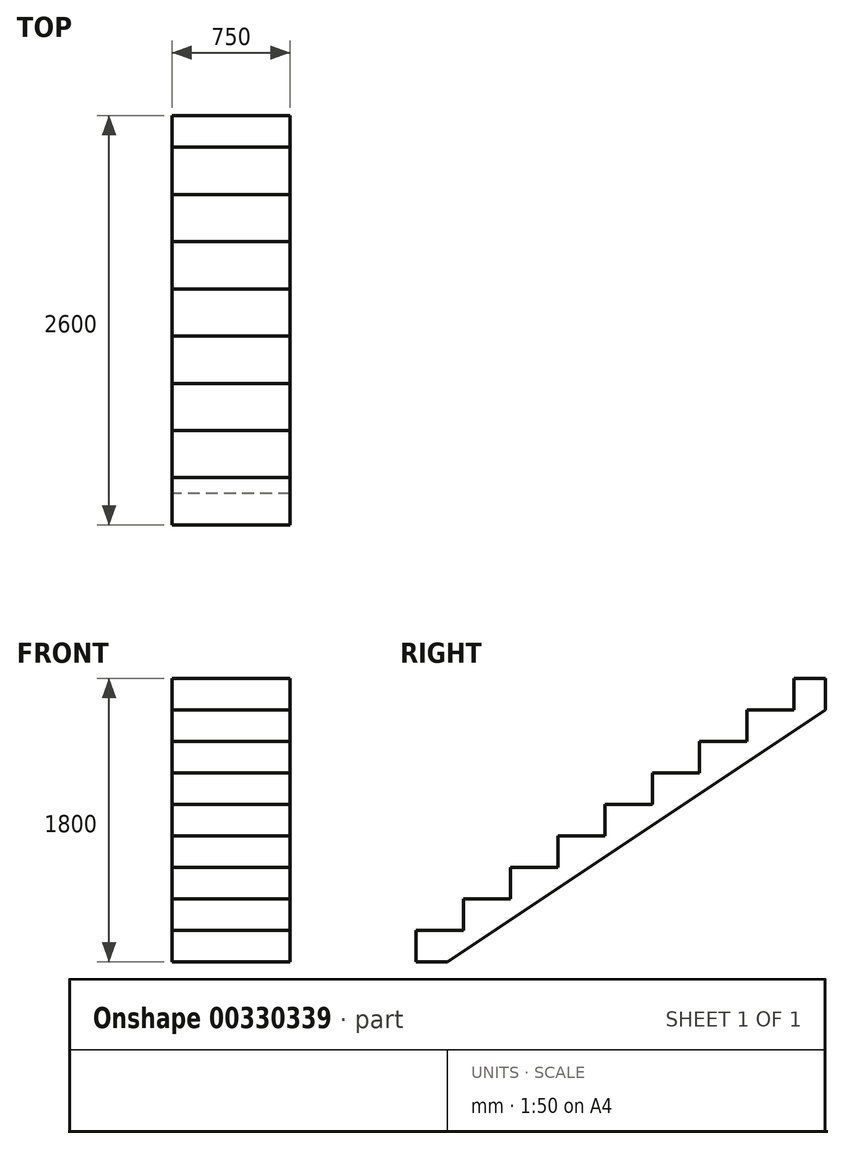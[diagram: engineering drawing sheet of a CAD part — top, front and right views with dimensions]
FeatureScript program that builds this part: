
annotation { "Feature Type Name" : "Feature", "Feature Type Description" : "" }
export const myFeature = defineFeature(function(context is Context, id is Id, definition is map)
    precondition{}
    {
        {
            var Q0;
            Q0=qCreatedBy(makeId("Right.planeOp"),FACE);
            var sketch = newSketch(context, id + "F0", { "sketchPlane" : qUnion([Q0])});
            skLineSegment(sketch, "E0", {"start": v(0, 0) * mm, "end": v(0, 200) * mm});
            skLineSegment(sketch, "E1", {"start": v(0, 200) * mm, "end": v(300, 200) * mm});
            skLineSegment(sketch, "E2", {"start": v(300, 200) * mm, "end": v(300, 400) * mm});
            skLineSegment(sketch, "E3", {"start": v(300, 400) * mm, "end": v(600, 400) * mm});
            skLineSegment(sketch, "E4", {"start": v(600, 400) * mm, "end": v(600, 600) * mm});
            skLineSegment(sketch, "E5", {"start": v(600, 600) * mm, "end": v(900, 600) * mm});
            skLineSegment(sketch, "E6", {"start": v(900, 600) * mm, "end": v(900, 800) * mm});
            skLineSegment(sketch, "E7", {"start": v(900, 800) * mm, "end": v(1200, 800) * mm});
            skLineSegment(sketch, "E8", {"start": v(1200, 800) * mm, "end": v(1200, 1000) * mm});
            skLineSegment(sketch, "E9", {"start": v(1200, 1000) * mm, "end": v(1500, 1000) * mm});
            skLineSegment(sketch, "E10", {"start": v(1500, 1000) * mm, "end": v(1500, 1200) * mm});
            skLineSegment(sketch, "E11", {"start": v(1500, 1200) * mm, "end": v(1800, 1200) * mm});
            skLineSegment(sketch, "E12", {"start": v(1800, 1200) * mm, "end": v(1800, 1400) * mm});
            skLineSegment(sketch, "E13", {"start": v(1800, 1400) * mm, "end": v(2100, 1400) * mm});
            skLineSegment(sketch, "E14", {"start": v(0, 0) * mm, "end": v(200, 0) * mm});
            skPoint(sketch, "E15.orphan", {"position": v(2100, 0) * mm});
            skLineSegment(sketch, "E16", {"start": v(2100, 1400) * mm, "end": v(2100, 1600) * mm});
            skLineSegment(sketch, "E17", {"start": v(2100, 1600) * mm, "end": v(2400, 1600) * mm});
            skLineSegment(sketch, "E18", {"start": v(2400, 1600) * mm, "end": v(2400, 1800) * mm});
            skLineSegment(sketch, "E19", {"start": v(2400, 1800) * mm, "end": v(2600, 1800) * mm});
            skLineSegment(sketch, "E20", {"start": v(2600, 1800) * mm, "end": v(2600, 1600) * mm});
            skLineSegment(sketch, "E21", {"start": v(200, 0) * mm, "end": v(2600, 1600) * mm});
            skSolve(sketch);
        }
        {
            var Q0;
            Q0=qSketchRegion(id+"F0",true);
            extrude(context, id + "F1", {"entities" : qUnion([Q0]), "depth" : 750 * mm});
        }
    });
